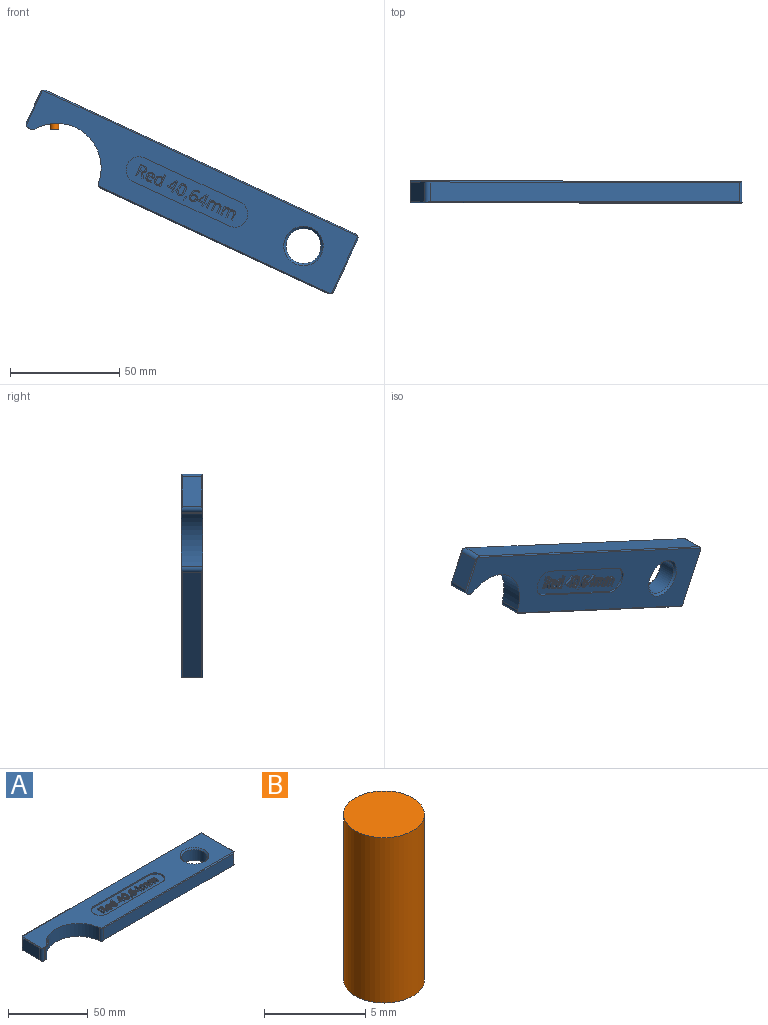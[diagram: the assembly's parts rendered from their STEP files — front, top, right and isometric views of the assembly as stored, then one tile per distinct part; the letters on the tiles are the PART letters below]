
ASSEMBLY  parts=2 mates=1
PART A: 248 faces, bbox 160x30x10 mm
  f0: cylinder r=20.32mm len=36.75mm, axis (0,0,-1), area 481.2mm2, adj f6,f7,f20,f25,f246
  f1: plane 60.11x12mm, normal (0,0,1), area 580.7mm2, adj f26,f27,f28,f29,f36,f37,f38,f39
  f2: plane 114.46x9mm, normal (0,-1,0), area 1030.1mm2, adj f10,f14,f20,f21
  f3: plane 26x9mm, normal (1,0,0), area 234mm2, adj f11,f15,f21,f22
  f4: plane 156x9mm, normal (0,1,0), area 1404mm2, adj f12,f16,f22,f23
  f5: plane 15x9mm, normal (-1,0,0), area 135mm2, adj f13,f17,f23,f24
  f6: plane 159x29mm, normal (0,0,1), area 3020.6mm2, adj f0,f8,f14,f15,f16,f17,f19,f20
  f7: plane 159x29mm, normal (0,0,-1), area 3710.9mm2, adj f0,f8,f10,f11,f12,f13,f18,f20
  f8: plane 10x1.17mm, normal (0,-1,0), area 11.7mm2, adj f6,f7,f24,f25
  f9: cylinder r=8mm len=16mm, axis (0,0,-1), area 402.1mm2, adj f18,f19
  f10: plane 117.1x0.5mm, normal (0,-0.71,-0.71), area 82.2mm2, adj f2,f7,f20,f21
  f11: plane 28.65x0.5mm, normal (0.71,0,-0.71), area 19.7mm2, adj f3,f7,f21,f22
  f12: plane 158.65x0.5mm, normal (0,0.71,-0.71), area 111.6mm2, adj f4,f7,f22,f23
  f13: plane 17.65x0.5mm, normal (-0.71,0,-0.71), area 11.9mm2, adj f5,f7,f23,f24
  f14: plane 117.1x0.5mm, normal (0,-0.71,0.71), area 82.2mm2, adj f2,f6,f20,f21
  f15: plane 28.65x0.5mm, normal (0.71,0,0.71), area 19.7mm2, adj f3,f6,f21,f22
  f16: plane 158.65x0.5mm, normal (0,0.71,0.71), area 111.6mm2, adj f4,f6,f22,f23
  f17: plane 17.65x0.5mm, normal (-0.71,0,0.71), area 11.9mm2, adj f5,f6,f23,f24
  f18: cone r=9mm half-angle=45deg, axis (0,0,-1), area 75.5mm2, adj f7,f9
  f19: cone r=8mm half-angle=45deg, axis (0,0,1), area 75.5mm2, adj f6,f9
  f20: cylinder r=2mm len=10mm, axis (0,0,-1), area 28.7mm2, adj f0,f2,f6,f7,f10,f14
  f21: cylinder r=2mm len=10mm, axis (0,0,1), area 29.5mm2, adj f2,f3,f6,f7,f10,f11,f14,f15
  f22: cylinder r=2mm len=10mm, axis (0,0,-1), area 29.5mm2, adj f3,f4,f6,f7,f11,f12,f15,f16
  f23: cylinder r=2mm len=10mm, axis (0,0,1), area 29.5mm2, adj f4,f5,f6,f7,f12,f13,f16,f17
  f24: cylinder r=2mm len=10mm, axis (0,0,1), area 30.5mm2, adj f5,f6,f7,f8,f13,f17
  f25: cylinder r=2mm len=10mm, axis (0,0,-1), area 19mm2, adj f0,f6,f7,f8
  f26: plane 48.11x1mm, normal (0,-1,0), area 48.1mm2, adj f1,f6,f27,f29
  f27: cylinder r=6mm len=12mm, axis (0,0,1), area 18.8mm2, adj f1,f6,f26,f28
  f28: plane 48.11x1mm, normal (0,1,0), area 48.1mm2, adj f1,f6,f27,f29
  f29: cylinder r=6mm len=12mm, axis (0,0,1), area 18.8mm2, adj f1,f6,f26,f28
  f30: plane 1x0.89mm, normal (0,1,0), area 0.9mm2, adj f31,f47,f48,f49
  f31: plane 2.12x1mm, normal (1,0,0), area 2.1mm2, adj f30,f32,f48,f49
  f32: plane 1x0.84mm, normal (0,-1,0), area 0.8mm2, adj f31,f33,f48,f49
  f33: extruded ~1.04x1mm, area 1.1mm2, adj f32,f34,f48,f49
  f34: extruded ~1x0.79mm, area 0.9mm2, adj f33,f35,f48,f49
  f35: extruded ~1x0.82mm, area 0.9mm2, adj f34,f47,f48,f49
  f36: plane 2.31x1mm, normal (1,0,0), area 2.3mm2, adj f1,f37,f46,f48
  f37: plane 1.16x1mm, normal (0,-1,0), area 1.2mm2, adj f1,f36,f38,f48
  f38: plane 2.31x1.34mm, normal (-0.86,-0.5,0), area 2.7mm2, adj f1,f37,f39,f48
  f39: plane 1x0.76mm, normal (0,-1,0), area 0.8mm2, adj f1,f38,f40,f48
  f40: plane 2.5x1.51mm, normal (0.86,0.52,0), area 2.9mm2, adj f1,f39,f41,f48
  f41: extruded ~1.49x1.12mm, area 2mm2, adj f1,f40,f42,f48
  f42: extruded ~1.18x1mm, area 1.3mm2, adj f1,f41,f43,f48
  f43: extruded ~1.51x1mm, area 1.6mm2, adj f1,f42,f44,f48
  f44: plane 1.52x1mm, normal (0,1,0), area 1.5mm2, adj f1,f43,f45,f48
  f45: plane 5.55x1mm, normal (-1,0,0), area 5.6mm2, adj f1,f44,f46,f48
  f46: plane 1x0.65mm, normal (0,-1,0), area 0.6mm2, adj f1,f36,f45,f48
  f47: extruded ~1x1mm, area 1.1mm2, adj f30,f35,f48,f49
  f48: plane 5.55x3.91mm, normal (0,0,1), area 9.2mm2, adj f30,f31,f32,f33,f34,f35,f36,f37
  f49: plane 2.21x2.12mm, normal (0,0,1), area 4.2mm2, adj f30,f31,f32,f33,f34,f35,f47
  f50: extruded ~1x0.8mm, area 0.9mm2, adj f51,f68,f69,f70
  f51: extruded ~1x0.76mm, area 0.9mm2, adj f50,f52,f69,f70
  f52: extruded ~1x0.91mm, area 1mm2, adj f51,f53,f69,f70
  f53: plane 2.18x1mm, normal (0,1,0), area 2.2mm2, adj f52,f68,f69,f70
  f54: extruded ~1.46x1mm, area 1.6mm2, adj f1,f55,f67,f69
  f55: extruded ~1x0.72mm, area 0.7mm2, adj f1,f54,f56,f69
  f56: extruded ~1x0.63mm, area 0.7mm2, adj f1,f55,f57,f69
  f57: plane 1x0.56mm, normal (1,0,0), area 0.6mm2, adj f1,f56,f58,f69
  f58: extruded ~1.33x1mm, area 1.4mm2, adj f1,f57,f59,f69
  f59: extruded ~1x0.99mm, area 1.1mm2, adj f1,f58,f60,f69
  f60: extruded ~1.11x1mm, area 1.2mm2, adj f1,f59,f61,f69
  f61: plane 2.87x1mm, normal (0,-1,0), area 2.9mm2, adj f1,f60,f62,f69
  f62: plane 1x0.4mm, normal (1,0,0), area 0.4mm2, adj f1,f61,f63,f69
  f63: extruded ~1.36x1mm, area 1.5mm2, adj f1,f62,f64,f69
  f64: extruded ~1.24x1mm, area 1.4mm2, adj f1,f63,f65,f69
  f65: extruded ~1.33x1mm, area 1.5mm2, adj f1,f64,f66,f69
  f66: extruded ~1.6x1mm, area 1.7mm2, adj f1,f65,f67,f69
  f67: extruded ~1.56x1mm, area 1.7mm2, adj f1,f54,f66,f69
  f68: extruded ~1x0.9mm, area 1mm2, adj f50,f53,f69,f70
  f69: plane 4.32x3.52mm, normal (0,0,1), area 6.9mm2, adj f50,f51,f52,f53,f54,f55,f56,f57
  f70: plane 2.18x1.23mm, normal (0,0,1), area 2.2mm2, adj f50,f51,f52,f53,f68
  f71: extruded ~1x0.94mm, area 1mm2, adj f72,f94,f95,f96
  f72: extruded ~1x0.86mm, area 1mm2, adj f71,f73,f95,f96
  f73: extruded ~1.2x1mm, area 1.3mm2, adj f72,f74,f95,f96
  f74: extruded ~1.22x1mm, area 1.3mm2, adj f73,f75,f95,f96
  f75: extruded ~1x0.85mm, area 1mm2, adj f74,f76,f95,f96
  f76: extruded ~1x0.94mm, area 1.1mm2, adj f75,f77,f95,f96
  f77: extruded ~1.26x1mm, area 1.3mm2, adj f76,f78,f95,f96
  f78: plane 1x0.13mm, normal (-1,0,0), area 0.1mm2, adj f77,f94,f95,f96
  f79: plane 1x0.03mm, normal (0,-1,0), area 0mm2, adj f1,f80,f93,f95
  f80: plane 1x0.56mm, normal (-0.99,-0.15,0), area 0.6mm2, adj f1,f79,f81,f95
  f81: plane 1x0.51mm, normal (0,-1,0), area 0.5mm2, adj f1,f80,f82,f95
  f82: plane 5.91x1mm, normal (1,0,0), area 5.9mm2, adj f1,f81,f83,f95
  f83: plane 1x0.63mm, normal (0,1,0), area 0.6mm2, adj f1,f82,f84,f95
  f84: plane 1.69x1mm, normal (-1,0,0), area 1.7mm2, adj f1,f83,f85,f95
  f85: plane 1x0.29mm, normal (-1,-0.05,0), area 0.3mm2, adj f1,f84,f86,f95
  f86: plane 1x0.3mm, normal (-1,-0.09,0), area 0.3mm2, adj f1,f85,f87,f95
  f87: plane 1x0.05mm, normal (0,1,0), area 0mm2, adj f1,f86,f88,f95
  f88: extruded ~1.3x1mm, area 1.5mm2, adj f1,f87,f89,f95
  f89: extruded ~1.27x1mm, area 1.4mm2, adj f1,f88,f90,f95
  f90: extruded ~1.6x1mm, area 1.7mm2, adj f1,f89,f91,f95
  f91: extruded ~1.59x1mm, area 1.7mm2, adj f1,f90,f92,f95
  f92: extruded ~1.27x1mm, area 1.4mm2, adj f1,f91,f93,f95
  f93: extruded ~1.31x1mm, area 1.5mm2, adj f1,f79,f92,f95
  f94: extruded ~1.13x1mm, area 1.2mm2, adj f71,f78,f95,f96
  f95: plane 5.99x3.66mm, normal (0,0,1), area 8.4mm2, adj f71,f72,f73,f74,f75,f76,f77,f78
  f96: plane 3.26x2.38mm, normal (0,0,1), area 6.5mm2, adj f71,f72,f73,f74,f75,f76,f77,f78
  f97: plane 1.85x1mm, normal (-1,0,0), area 1.8mm2, adj f98,f113,f114,f115
  f98: plane 2.07x1mm, normal (0,1,0), area 2.1mm2, adj f97,f99,f114,f115
  f99: plane 2.47x1.74mm, normal (0.82,-0.58,0), area 3mm2, adj f98,f100,f114,f115
  f100: extruded ~1x0.6mm, area 0.7mm2, adj f99,f101,f114,f115
  f101: plane 1x0.03mm, normal (0,-1,0), area 0mm2, adj f100,f113,f114,f115
  f102: plane 1x0.82mm, normal (0,-1,0), area 0.8mm2, adj f1,f103,f112,f114
  f103: plane 1x0.57mm, normal (1,0,0), area 0.6mm2, adj f1,f102,f104,f114
  f104: plane 1x0.82mm, normal (0,1,0), area 0.8mm2, adj f1,f103,f105,f114
  f105: plane 3.73x1mm, normal (1,0,0), area 3.7mm2, adj f1,f104,f106,f114
  f106: plane 1x0.67mm, normal (0,1,0), area 0.7mm2, adj f1,f105,f107,f114
  f107: plane 3.76x2.64mm, normal (-0.82,0.57,0), area 4.6mm2, adj f1,f106,f108,f114
  f108: plane 1x0.55mm, normal (-1,0,0), area 0.6mm2, adj f1,f107,f109,f114
  f109: plane 2.7x1mm, normal (0,-1,0), area 2.7mm2, adj f1,f108,f110,f114
  f110: plane 1.28x1mm, normal (-1,0,0), area 1.3mm2, adj f1,f109,f111,f114
  f111: plane 1x0.6mm, normal (0,-1,0), area 0.6mm2, adj f1,f110,f112,f114
  f112: plane 1.28x1mm, normal (1,0,0), area 1.3mm2, adj f1,f102,f111,f114
  f113: extruded ~1.23x1mm, area 1.2mm2, adj f97,f101,f114,f115
  f114: plane 5.58x4.13mm, normal (0,0,1), area 7.4mm2, adj f97,f98,f99,f100,f101,f102,f103,f104
  f115: plane 3.07x2.11mm, normal (0,0,1), area 3.1mm2, adj f97,f98,f99,f100,f101,f113
  f116: extruded ~1.76x1mm, area 1.8mm2, adj f117,f131,f132,f133
  f117: extruded ~1.76x1mm, area 1.8mm2, adj f116,f118,f132,f133
  f118: extruded ~1x0.91mm, area 1.1mm2, adj f117,f119,f132,f133
  f119: extruded ~1x0.91mm, area 1.1mm2, adj f118,f120,f132,f133
  f120: extruded ~1.75x1mm, area 1.8mm2, adj f119,f121,f132,f133
  f121: extruded ~1.76x1mm, area 1.8mm2, adj f120,f122,f132,f133
  f122: extruded ~1x0.91mm, area 1.1mm2, adj f121,f131,f132,f133
  f123: extruded ~2.15x1mm, area 2.2mm2, adj f1,f124,f130,f132
  f124: extruded ~2.12x1mm, area 2.2mm2, adj f1,f123,f125,f132
  f125: extruded ~1.37x1mm, area 1.6mm2, adj f1,f124,f126,f132
  f126: extruded ~1.38x1mm, area 1.6mm2, adj f1,f125,f127,f132
  f127: extruded ~2.15x1mm, area 2.2mm2, adj f1,f126,f128,f132
  f128: extruded ~2.13x1mm, area 2.2mm2, adj f1,f127,f129,f132
  f129: extruded ~1.36x1mm, area 1.6mm2, adj f1,f128,f130,f132
  f130: extruded ~1.39x1mm, area 1.6mm2, adj f1,f123,f129,f132
  f131: extruded ~1x0.91mm, area 1.1mm2, adj f116,f122,f132,f133
  f132: plane 5.72x3.67mm, normal (0,0,1), area 8.1mm2, adj f116,f117,f118,f119,f120,f121,f122,f123
  f133: plane 4.63x2.39mm, normal (0,0,1), area 9.3mm2, adj f116,f117,f118,f119,f120,f121,f122,f131
  f134: plane 1x0.09mm, normal (0.84,0.55,0), area 0.1mm2, adj f1,f135,f140,f141
  f135: plane 1x0.69mm, normal (0,1,0), area 0.7mm2, adj f1,f134,f136,f141
  f136: extruded ~1x0.93mm, area 0.9mm2, adj f1,f135,f137,f141
  f137: extruded ~1x0.98mm, area 1mm2, adj f1,f136,f138,f141
  f138: plane 1x0.48mm, normal (0,-1,0), area 0.5mm2, adj f1,f137,f139,f141
  f139: extruded ~1x0.94mm, area 1mm2, adj f1,f138,f140,f141
  f140: extruded ~1x0.88mm, area 0.9mm2, adj f1,f134,f139,f141
  f141: plane 1.91x1.15mm, normal (0,0,1), area 1.2mm2, adj f134,f135,f136,f137,f138,f139,f140
  f142: extruded ~1x0.84mm, area 0.9mm2, adj f143,f166,f167,f168
  f143: extruded ~1x0.64mm, area 0.7mm2, adj f142,f144,f167,f168
  f144: extruded ~1x0.54mm, area 0.7mm2, adj f143,f145,f167,f168
  f145: extruded ~1x0.73mm, area 0.8mm2, adj f144,f146,f167,f168
  f146: extruded ~1x0.51mm, area 0.5mm2, adj f145,f147,f167,f168
  f147: extruded ~1x0.45mm, area 0.6mm2, adj f146,f148,f167,f168
  f148: extruded ~1x0.63mm, area 0.6mm2, adj f147,f149,f167,f168
  f149: extruded ~1x0.83mm, area 0.9mm2, adj f148,f150,f167,f168
  f150: extruded ~1x0.87mm, area 0.9mm2, adj f149,f166,f167,f168
  f151: extruded ~2.45x1mm, area 2.6mm2, adj f1,f152,f165,f167
  f152: extruded ~1.8x1mm, area 1.9mm2, adj f1,f151,f153,f167
  f153: extruded ~1.37x1mm, area 1.6mm2, adj f1,f152,f154,f167
  f154: extruded ~1.28x1mm, area 1.4mm2, adj f1,f153,f155,f167
  f155: extruded ~1.36x1mm, area 1.5mm2, adj f1,f154,f156,f167
  f156: extruded ~1.23x1mm, area 1.3mm2, adj f1,f155,f157,f167
  f157: extruded ~1.18x1mm, area 1.3mm2, adj f1,f156,f158,f167
  f158: extruded ~1.32x1mm, area 1.5mm2, adj f1,f157,f159,f167
  f159: plane 1x0.05mm, normal (0,1,0), area 0mm2, adj f1,f158,f160,f167
  f160: extruded ~1.75x1mm, area 1.9mm2, adj f1,f159,f161,f167
  f161: extruded ~1.36x1mm, area 1.5mm2, adj f1,f160,f162,f167
  f162: extruded ~1x0.67mm, area 0.7mm2, adj f1,f161,f163,f167
  f163: plane 1x0.54mm, normal (1,0,0), area 0.5mm2, adj f1,f162,f164,f167
  f164: extruded ~1x0.68mm, area 0.7mm2, adj f1,f163,f165,f167
  f165: extruded ~1.88x1mm, area 2.1mm2, adj f1,f151,f164,f167
  f166: extruded ~1x0.98mm, area 1mm2, adj f142,f150,f167,f168
  f167: plane 5.71x3.62mm, normal (0,0,1), area 8mm2, adj f142,f143,f144,f145,f146,f147,f148,f149
  f168: plane 2.5x2.35mm, normal (0,0,1), area 4.8mm2, adj f142,f143,f144,f145,f146,f147,f148,f149
  f169: plane 1.85x1mm, normal (-1,0,0), area 1.8mm2, adj f170,f185,f186,f187
  f170: plane 2.07x1mm, normal (0,1,0), area 2.1mm2, adj f169,f171,f186,f187
  f171: plane 2.47x1.74mm, normal (0.82,-0.58,0), area 3mm2, adj f170,f172,f186,f187
  f172: extruded ~1x0.6mm, area 0.7mm2, adj f171,f173,f186,f187
  f173: plane 1x0.03mm, normal (0,-1,0), area 0mm2, adj f172,f185,f186,f187
  f174: plane 1x0.82mm, normal (0,-1,0), area 0.8mm2, adj f1,f175,f184,f186
  f175: plane 1x0.57mm, normal (1,0,0), area 0.6mm2, adj f1,f174,f176,f186
  f176: plane 1x0.82mm, normal (0,1,0), area 0.8mm2, adj f1,f175,f177,f186
  f177: plane 3.73x1mm, normal (1,0,0), area 3.7mm2, adj f1,f176,f178,f186
  f178: plane 1x0.67mm, normal (0,1,0), area 0.7mm2, adj f1,f177,f179,f186
  f179: plane 3.76x2.64mm, normal (-0.82,0.57,0), area 4.6mm2, adj f1,f178,f180,f186
  f180: plane 1x0.55mm, normal (-1,0,0), area 0.6mm2, adj f1,f179,f181,f186
  f181: plane 2.7x1mm, normal (0,-1,0), area 2.7mm2, adj f1,f180,f182,f186
  f182: plane 1.28x1mm, normal (-1,0,0), area 1.3mm2, adj f1,f181,f183,f186
  f183: plane 1x0.6mm, normal (0,-1,0), area 0.6mm2, adj f1,f182,f184,f186
  f184: plane 1.28x1mm, normal (1,0,0), area 1.3mm2, adj f1,f174,f183,f186
  f185: extruded ~1.23x1mm, area 1.2mm2, adj f169,f173,f186,f187
  f186: plane 5.58x4.13mm, normal (0,0,1), area 7.4mm2, adj f169,f170,f171,f172,f173,f174,f175,f176
  f187: plane 3.07x2.11mm, normal (0,0,1), area 3.1mm2, adj f169,f170,f171,f172,f173,f185
  f188: plane 2.71x1mm, normal (-1,0,0), area 2.7mm2, adj f1,f189,f215,f216
  f189: plane 1x0.63mm, normal (0,-1,0), area 0.6mm2, adj f1,f188,f190,f216
  f190: plane 2.72x1mm, normal (1,0,0), area 2.7mm2, adj f1,f189,f191,f216
  f191: extruded ~1.16x1mm, area 1.2mm2, adj f1,f190,f192,f216
  f192: extruded ~1.06x1mm, area 1.1mm2, adj f1,f191,f193,f216
  f193: extruded ~1x0.81mm, area 0.8mm2, adj f1,f192,f194,f216
  f194: extruded ~1x0.54mm, area 0.8mm2, adj f1,f193,f195,f216
  f195: plane 1x0.03mm, normal (0,1,0), area 0mm2, adj f1,f194,f196,f216
  f196: extruded ~1.28x1mm, area 1.6mm2, adj f1,f195,f197,f216
  f197: extruded ~1x0.73mm, area 0.8mm2, adj f1,f196,f198,f216
  f198: extruded ~1x0.5mm, area 0.7mm2, adj f1,f197,f199,f216
  f199: plane 1x0.03mm, normal (0,1,0), area 0mm2, adj f1,f198,f200,f216
  f200: plane 1x0.57mm, normal (0.98,0.18,0), area 0.6mm2, adj f1,f199,f201,f216
  f201: plane 1x0.51mm, normal (0,1,0), area 0.5mm2, adj f1,f200,f202,f216
  f202: plane 4.16x1mm, normal (-1,0,0), area 4.2mm2, adj f1,f201,f203,f216
  f203: plane 1x0.63mm, normal (0,-1,0), area 0.6mm2, adj f1,f202,f204,f216
  f204: plane 2.18x1mm, normal (1,0,0), area 2.2mm2, adj f1,f203,f205,f216
  f205: extruded ~1.16x1mm, area 1.2mm2, adj f1,f204,f206,f216
  f206: extruded ~1x0.87mm, area 1mm2, adj f1,f205,f207,f216
  f207: extruded ~1x0.67mm, area 0.7mm2, adj f1,f206,f208,f216
  f208: extruded ~1x0.75mm, area 0.8mm2, adj f1,f207,f209,f216
  f209: plane 2.71x1mm, normal (-1,0,0), area 2.7mm2, adj f1,f208,f210,f216
  f210: plane 1x0.63mm, normal (0,-1,0), area 0.6mm2, adj f1,f209,f211,f216
  f211: plane 2.33x1mm, normal (1,0,0), area 2.3mm2, adj f1,f210,f212,f216
  f212: extruded ~1.04x1mm, area 1.1mm2, adj f1,f211,f213,f216
  f213: extruded ~1x0.87mm, area 1mm2, adj f1,f212,f214,f216
  f214: extruded ~1x0.66mm, area 0.7mm2, adj f1,f213,f215,f216
  f215: extruded ~1x0.75mm, area 0.8mm2, adj f1,f188,f214,f216
  f216: plane 5.94x4.24mm, normal (0,0,1), area 9.8mm2, adj f188,f189,f190,f191,f192,f193,f194,f195
  f217: plane 2.71x1mm, normal (-1,0,0), area 2.7mm2, adj f1,f218,f244,f245
  f218: plane 1x0.63mm, normal (0,-1,0), area 0.6mm2, adj f1,f217,f219,f245
  f219: plane 2.72x1mm, normal (1,0,0), area 2.7mm2, adj f1,f218,f220,f245
  f220: extruded ~1.16x1mm, area 1.2mm2, adj f1,f219,f221,f245
  f221: extruded ~1.06x1mm, area 1.1mm2, adj f1,f220,f222,f245
  f222: extruded ~1x0.81mm, area 0.8mm2, adj f1,f221,f223,f245
  f223: extruded ~1x0.54mm, area 0.8mm2, adj f1,f222,f224,f245
  f224: plane 1x0.03mm, normal (0,1,0), area 0mm2, adj f1,f223,f225,f245
  f225: extruded ~1.28x1mm, area 1.6mm2, adj f1,f224,f226,f245
  f226: extruded ~1x0.73mm, area 0.8mm2, adj f1,f225,f227,f245
  f227: extruded ~1x0.5mm, area 0.7mm2, adj f1,f226,f228,f245
  f228: plane 1x0.03mm, normal (0,1,0), area 0mm2, adj f1,f227,f229,f245
  f229: plane 1x0.57mm, normal (0.98,0.18,0), area 0.6mm2, adj f1,f228,f230,f245
  f230: plane 1x0.51mm, normal (0,1,0), area 0.5mm2, adj f1,f229,f231,f245
  f231: plane 4.16x1mm, normal (-1,0,0), area 4.2mm2, adj f1,f230,f232,f245
  f232: plane 1x0.63mm, normal (0,-1,0), area 0.6mm2, adj f1,f231,f233,f245
  f233: plane 2.18x1mm, normal (1,0,0), area 2.2mm2, adj f1,f232,f234,f245
  f234: extruded ~1.16x1mm, area 1.2mm2, adj f1,f233,f235,f245
  f235: extruded ~1x0.87mm, area 1mm2, adj f1,f234,f236,f245
  f236: extruded ~1x0.67mm, area 0.7mm2, adj f1,f235,f237,f245
  f237: extruded ~1x0.75mm, area 0.8mm2, adj f1,f236,f238,f245
  f238: plane 2.71x1mm, normal (-1,0,0), area 2.7mm2, adj f1,f237,f239,f245
  f239: plane 1x0.63mm, normal (0,-1,0), area 0.6mm2, adj f1,f238,f240,f245
  f240: plane 2.33x1mm, normal (1,0,0), area 2.3mm2, adj f1,f239,f241,f245
  f241: extruded ~1.04x1mm, area 1.1mm2, adj f1,f240,f242,f245
  f242: extruded ~1x0.87mm, area 1mm2, adj f1,f241,f243,f245
  f243: extruded ~1x0.66mm, area 0.7mm2, adj f1,f242,f244,f245
  f244: extruded ~1x0.75mm, area 0.8mm2, adj f1,f217,f243,f245
  f245: plane 5.94x4.24mm, normal (0,0,1), area 9.8mm2, adj f217,f218,f219,f220,f221,f222,f223,f224
  f246: cylinder r=2mm len=8.24mm, axis (-0.42,0.91,0), area 88.9mm2, adj f0,f247
  f247: plane 4x3.63mm, normal (0.42,-0.91,0), area 12.6mm2, adj f246
PART B: 3 faces, bbox 4x4x10 mm
  f0: cylinder r=2mm len=10mm, axis (0,0,-1), area 125.7mm2, adj f1,f2
  f1: plane 4x4mm, normal (0,0,1), area 12.6mm2, adj f0
  f2: plane 4x4mm, normal (0,0,-1), area 12.6mm2, adj f0
PLACE A rot(axis=(0.95,0.21,-0.21),92.7deg) t=(11.29,-30.31,-43.62)mm
PLACE B t=(-49.33,-35.31,-15.24)mm
MATE fastened A.f246 <-> B.f0  axis (0,0,-1) through (-49.33,-35.31,-5.24)mm
